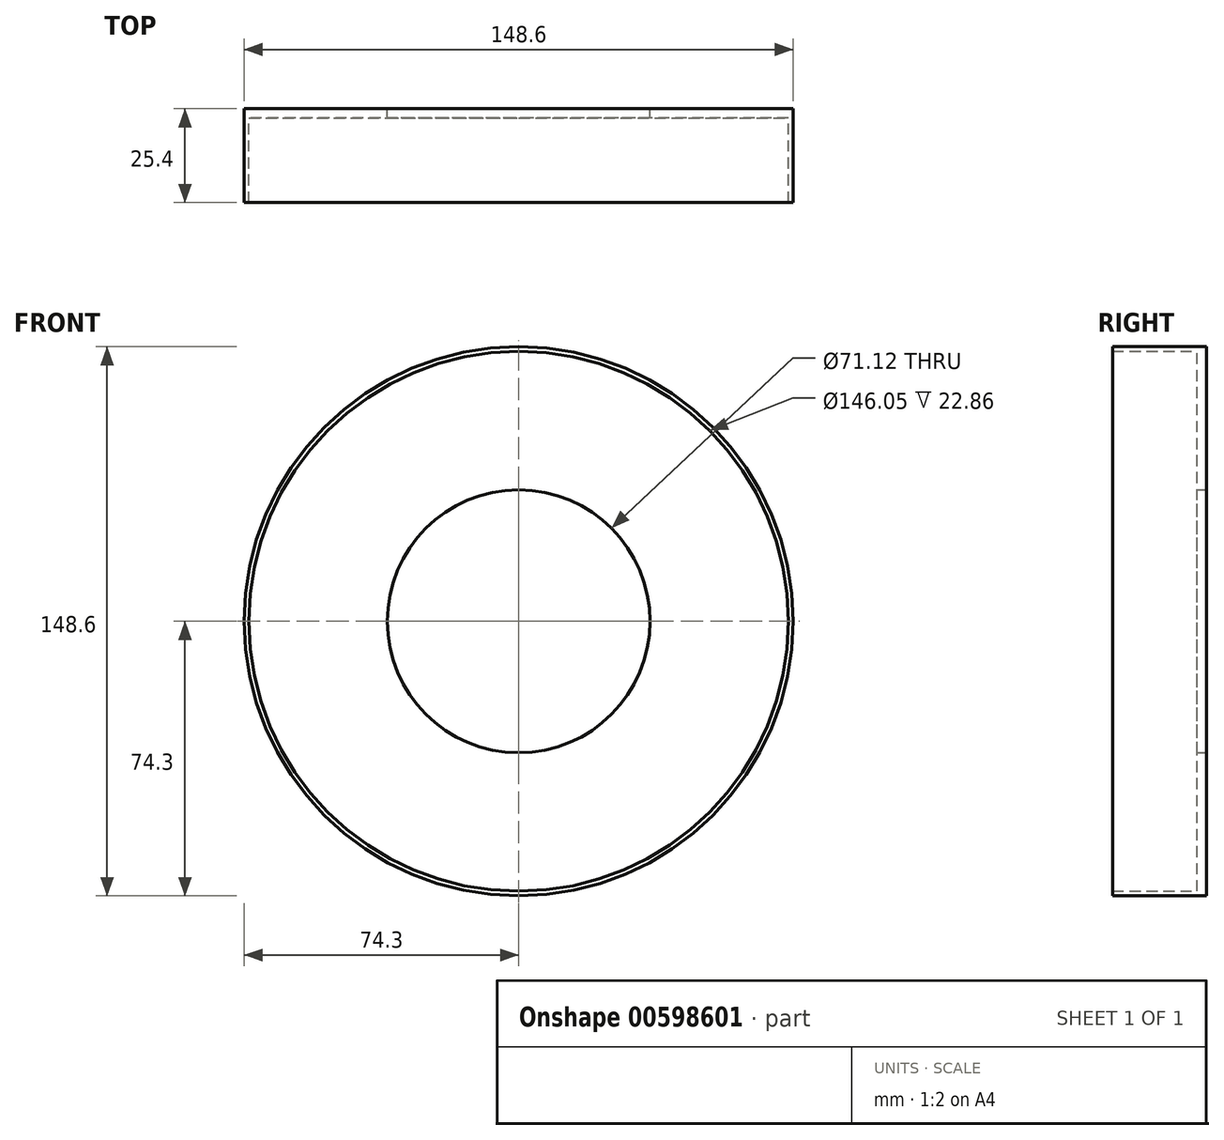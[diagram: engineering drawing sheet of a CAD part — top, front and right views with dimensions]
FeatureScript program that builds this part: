
annotation { "Feature Type Name" : "Feature", "Feature Type Description" : "" }
export const myFeature = defineFeature(function(context is Context, id is Id, definition is map)
    precondition{}
    {
        {
            var Q0;
            Q0=qCreatedBy(makeId("Front.planeOp"),FACE);
            var sketch = newSketch(context, id + "F0", { "sketchPlane" : qUnion([Q0])});
            skCircle(sketch, "E0", {"center": v(0, 0) * mm, "radius": 73.03 * mm});
            skCircle(sketch, "E1", {"center": v(0, 0) * mm, "radius": 35.56 * mm});
            skCircle(sketch, "E2", {"center": v(0, 0) * mm, "radius": 74.3 * mm});
            skSolve(sketch);
        }
        {
            var Q0;
            Q0 = qSketchRegion(id + "F0", true);
            var Q1;
            Q1=makeQuery(id+"F0.imprint","IMPRINT",FACE,{"disambiguationData":[TD([[makeQuery(id+"F0.imprint","IMPRINT",EDGE,{"derivedFrom":sQuery(id+"F0.wireOp",EDGE,"E0")}),1.0]])]});
            extrude(context, id + "F1", {"entities" : qUnion([Q0, Q1]), "depth" : 2.54 * mm, "offsetDistance" : 25.4 * mm});
        }
        {
            var Q0;
            Q0=makeQuery(id+"F0.imprint","IMPRINT",FACE,{"disambiguationData":[TD([[makeQuery(id+"F0.imprint","IMPRINT",EDGE,{"derivedFrom":sQuery(id+"F0.wireOp",EDGE,"E0")}),-1.0]])]});
            extrude(context, id + "F2", {"entities" : qUnion([Q0]), "operationType" : NewBodyOperationType.ADD, "depth" : 25.4 * mm, "offsetDistance" : 25.4 * mm});
        }
    });
